# Revit family: Steel-Entrance-Doors_Soho-P12-7ft0in_Novatech
name_source: partatom
category: Doors
units: mm (PartAtom-declared; Revit-internal decimal feet)

## family parameters
Always vertical = Yes
Classification Number = 23.30.10.00
Cut with Voids When Loaded = No
Host = Wall
Room Calculation Point = No
Shared = No

## types (3) — shared parameters
Analytic Construction = <None>
Bottom Distance = 11.5000"
CAD Details = https://www.arcat.com
Define Thermal Properties by = Schematic Type
Door Height = 84.0000"
Embossment Height = 13.0000"
Embossment Length = 23.0000"
Frame Thickness = 1.4850"
Function = Interior
Height = 84.0000"
Keynote = 08 13 00
Manufacturer = Novatech
Model = Soho
Product Page URL = https://www.arcat.com
Specification = https://www.arcat.com
Thickness = 1.7300"
Top Distance = 7.5000"
URL = https://www.groupenovatech.com
Wall Closure = By host

## per-type parameters (varying)
| type | B - Distance | C - Distance | Door Width | Width |
| 2' 8" x 7' 0" | 4.3100" | 4.4400" | 31.7500" | 31.7500" |
| 2' 10" x 7' 0" | 5.3100" | 5.4400" | 33.7500" | 33.7500" |
| 3' 0" x 7' 0" | 6.3100" | 6.4400" | 35.7500" | 35.7500" |

## geometry (parser evidence)
native form markers: Sweep x3
no freeform markers — native parametric forms only
